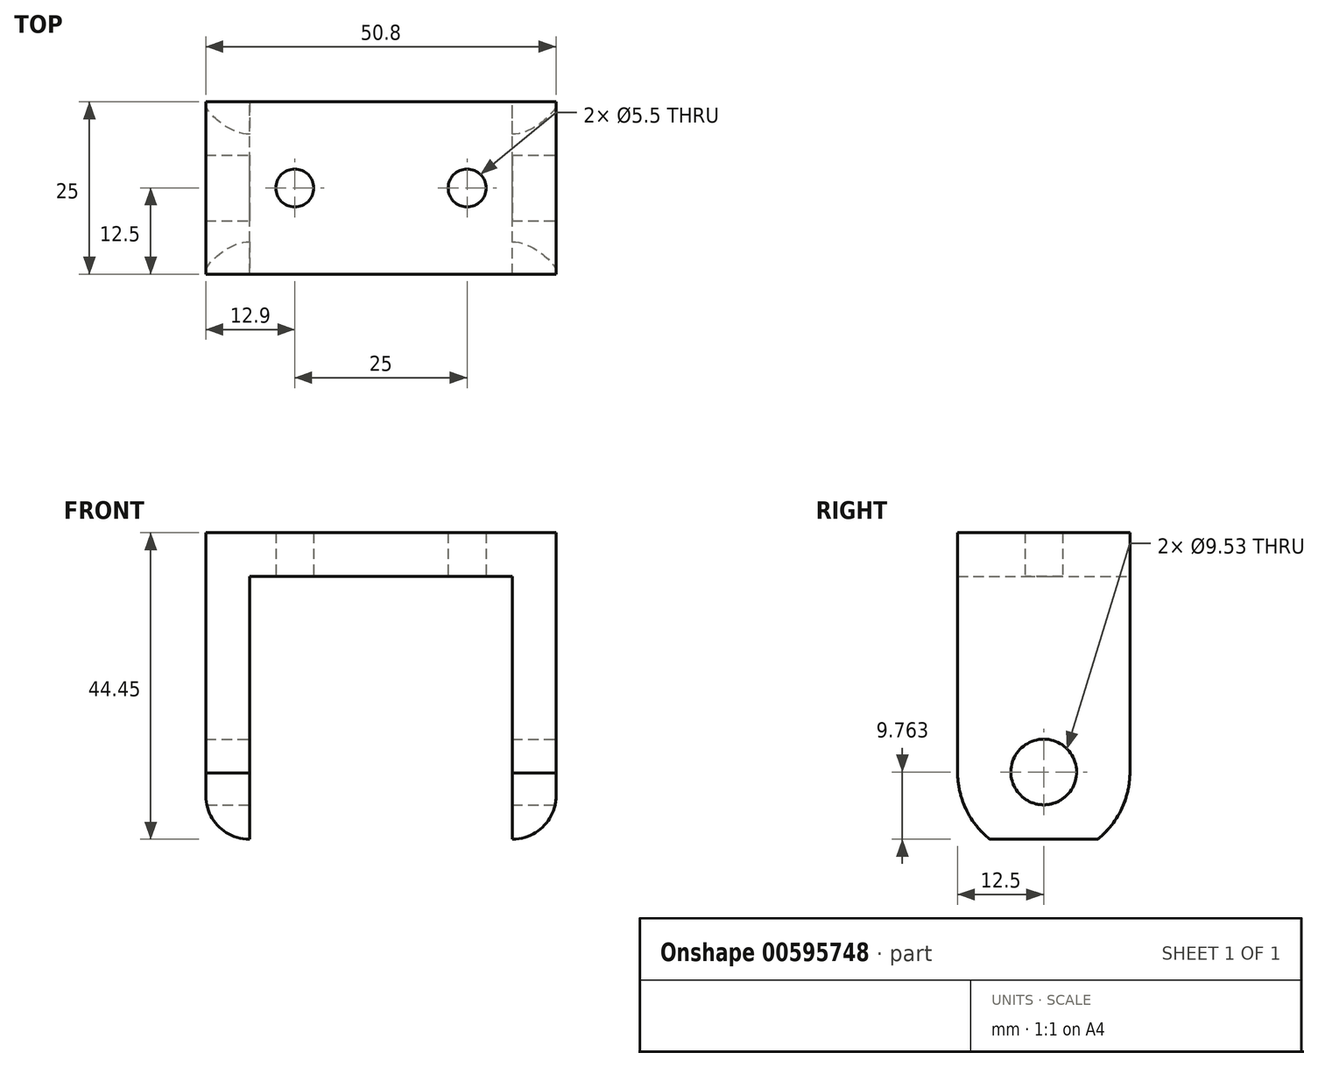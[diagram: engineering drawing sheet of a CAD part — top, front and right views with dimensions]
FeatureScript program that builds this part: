
annotation { "Feature Type Name" : "Feature", "Feature Type Description" : "" }
export const myFeature = defineFeature(function(context is Context, id is Id, definition is map)
    precondition{}
    {
        {
            var Q0;
            Q0=qCreatedBy(makeId("Front.planeOp"),FACE);
            var sketch = newSketch(context, id + "F0", { "sketchPlane" : qUnion([Q0])});
            skLineSegment(sketch, "E0", {"start": v(0, 0) * mm, "end": v(25.4, 0) * mm});
            skLineSegment(sketch, "E1", {"start": v(25.4, 0) * mm, "end": v(25.4, -38.1) * mm});
            skLineSegment(sketch, "E2", {"start": v(0, 0) * mm, "end": v(0, -6.35) * mm});
            skLineSegment(sketch, "E3", {"start": v(0, -6.35) * mm, "end": v(19.05, -6.35) * mm});
            skLineSegment(sketch, "E4", {"start": v(19.05, -6.35) * mm, "end": v(19.05, -44.45) * mm});
            skArc(sketch, "E5", {"start": v(25.4, -38.1) * mm, "mid": v(23.54, -42.6) * mm, "end": v(19.05, -44.45) * mm});
            skSolve(sketch);
        }
        {
            var Q0;
            Q0=makeQuery(id+"F0.imprint","IMPRINT",FACE,{"disambiguationData":[TD([[makeQuery(id+"F0.imprint","IMPRINT",EDGE,{"derivedFrom":sQuery(id+"F0.wireOp",EDGE,"E0")}),-1.0]])]});
            extrude(context, id + "F1", {"entities" : qUnion([Q0]), "depth" : 25 * mm, "offsetDistance" : 25 * mm, "symmetric" : true});
        }
        {
            var Q0;
            Q0=makeQuery(id+"F1.opExtrude","SWEPT_FACE",FACE,{"disambiguationData":[OSD([sQuery(id+"F0.wireOp",EDGE,"E1")])]});
            var sketch = newSketch(context, id + "F2", { "sketchPlane" : qUnion([Q0])});
            skCircle(sketch, "E6", {"center": v(0, -244.21) * mm, "radius": 48.26 * mm});
            skCircle(sketch, "E7", {"center": v(0, -34.69) * mm, "radius": 4.76 * mm});
            skLineSegment(sketch, "E8.0", {"start": v(-12.5, -38.1) * mm, "end": v(12.5, -38.1) * mm, "construction": true});
            skSolve(sketch);
        }
        {
            var Q0;
            Q0=makeQuery(id+"F1.opExtrude","SWEPT_BODY",BODY,{"disambiguationData":[OSD([sQuery(id+"F0.wireOp",EDGE,"E0"),sQuery(id+"F0.wireOp",EDGE,"gVfCCOhb-I9gK-rC6D-NhWc-HWcXAPihaaI6"),sQuery(id+"F0.wireOp",EDGE,"C00b1ODD-DF0h-D2k2-2Klx-7LYLyqmDbQ7s"),sQuery(id+"F0.wireOp",EDGE,"9iutq9FK-PZdQ-onyf-OhcQ-VJXVPDdDGBpG"),sQuery(id+"F0.wireOp",EDGE,"9qtEYHGX-QkRf-Tpsb-zOfX-uEoeoekVGbbH"),sQuery(id+"F0.wireOp",EDGE,"ldGhnjMj-BCIG-oYZQ-yVlH-KHscERw0lFE9")])]});
            var Q1;
            Q1=qCreatedBy(makeId("Right.planeOp"),FACE);
            mirror(context, id + "F3", {"operationType" : NewBodyOperationType.ADD, "entities" : qUnion([Q0]), "mirrorPlane" : qUnion([Q1])});
        }
        {
            var Q0;
            Q0=qSketchRegion(id+"F2",true);
            extrude(context, id + "F4", {"entities" : qUnion([Q0]), "operationType" : NewBodyOperationType.REMOVE, "endBound" : BoundingType.THROUGH_ALL, "oppositeDirection" : true, "depth" : 25 * mm, "offsetDistance" : 25 * mm});
        }
        {
            var Q0;
            Q0=makeQuery(id+"F1.opExtrude","SWEPT_FACE",FACE,{"disambiguationData":[OSD([sQuery(id+"F0.wireOp",EDGE,"E1")])]});
            var sketch = newSketch(context, id + "F5", { "sketchPlane" : qUnion([Q0])});
            skArc(sketch, "E9", {"start": v(-12.5, -34.86) * mm, "mid": v(0.17, -47.19) * mm, "end": v(12.5, -34.52) * mm});
            skLineSegment(sketch, "E10", {"start": v(-12.5, -34.86) * mm, "end": v(-12.5, -48.7) * mm});
            skLineSegment(sketch, "E11", {"start": v(-12.5, -48.7) * mm, "end": v(13.1, -48.7) * mm});
            skLineSegment(sketch, "E12", {"start": v(13.1, -48.7) * mm, "end": v(12.5, -34.52) * mm});
            skSolve(sketch);
        }
        {
            var Q0;
            Q0 = qSketchRegion(id + "F5", true);
            extrude(context, id + "F6", {"entities" : qUnion([Q0]), "operationType" : NewBodyOperationType.REMOVE, "endBound" : BoundingType.THROUGH_ALL, "oppositeDirection" : true, "depth" : 25 * mm, "offsetDistance" : 25 * mm});
        }
        {
            var Q0;
            {var subQ0=makeQuery(id+"F1.opExtrude","SWEPT_FACE",FACE,{"disambiguationData":[OSD([sQuery(id+"F0.wireOp",EDGE,"E3")])]});Q0=makeQuery(id+"F3.boolean.opBoolean","MERGE",FACE,{"derivedFrom":[subQ0,makeQuery(id+"F3.opPattern","COPY",FACE,{"derivedFrom":subQ0,"instanceName":"1"})]});}
            var sketch = newSketch(context, id + "F7", { "sketchPlane" : qUnion([Q0])});
            skPoint(sketch, "E13", {"position": v(-12.5, 0) * mm});
            skPoint(sketch, "E14", {"position": v(12.5, 0) * mm});
            skSolve(sketch);
        }
        {
            var Q0;
            Q0=sQuery(id+"F7.wireOp",VERTEX,"E13");
            var Q1;
            Q1=sQuery(id+"F7.wireOp",VERTEX,"E14");
            var Q2;
            Q2=makeQuery(id+"F1.opExtrude","SWEPT_BODY",BODY,{"disambiguationData":[OSD([sQuery(id+"F0.wireOp",EDGE,"E0"),sQuery(id+"F0.wireOp",EDGE,"E1"),sQuery(id+"F0.wireOp",EDGE,"E2"),sQuery(id+"F0.wireOp",EDGE,"E3"),sQuery(id+"F0.wireOp",EDGE,"E4"),sQuery(id+"F0.wireOp",EDGE,"E5")])]});
            hole(context, id + "F8", {"style" : HoleStyle.SIMPLE, "endStyle" : HoleEndStyle.BLIND, "standardTappedOrClearance" : lookupTablePath({ "standard" : "ISO", "fit" : "Normal", "size" : "M5", "type" : "Clearance" }), "standardBlindInLast" : lookupTablePath({ "fit" : "Standard", "standard" : "ISO", "size" : "M5", "type" : "Clearance" }), "holeDiameter" : 5.5 * mm, "majorDiameter" : 5 * mm, "holeDepth" : 10 * mm, "isTappedThrough" : true, "tappedDepth" : 12 * mm, "tapClearance" : 3, "locations" : qUnion([Q0, Q1]), "scope" : qUnion([Q2])});
        }
    });
